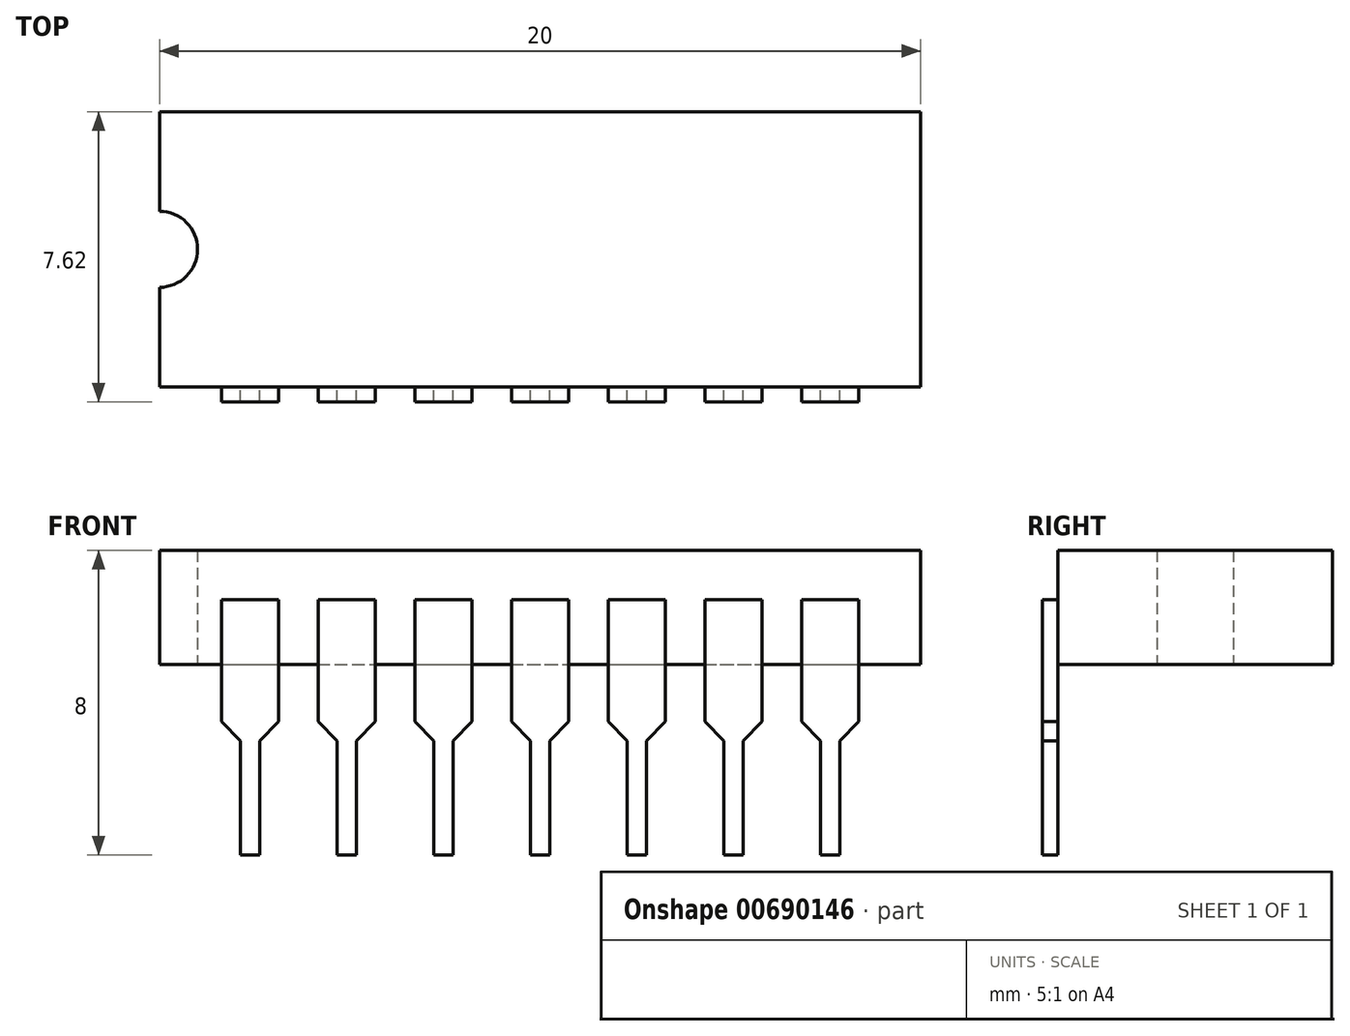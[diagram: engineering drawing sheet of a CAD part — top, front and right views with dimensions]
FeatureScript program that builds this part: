
annotation { "Feature Type Name" : "Feature", "Feature Type Description" : "" }
export const myFeature = defineFeature(function(context is Context, id is Id, definition is map)
    precondition{}
    {
        {
            var Q0;
            Q0=qCreatedBy(makeId("Top.planeOp"),FACE);
            var sketch = newSketch(context, id + "F0", { "sketchPlane" : qUnion([Q0])});
            skLineSegment(sketch, "E0.bottom", {"start": v(-10, 3.6) * mm, "end": v(10, 3.6) * mm});
            skLineSegment(sketch, "E0.top", {"start": v(-10, -3.6) * mm, "end": v(10, -3.6) * mm});
            skLineSegment(sketch, "E0.left", {"start": v(-10, 3.6) * mm, "end": v(-10, 1) * mm});
            skLineSegment(sketch, "E0.right", {"start": v(10, 3.6) * mm, "end": v(10, -3.6) * mm});
            skPoint(sketch, "E0.middle", {"position": v(0, 0) * mm});
            skArc(sketch, "E1", {"start": v(-10, 1) * mm, "mid": v(-9, 0) * mm, "end": v(-10, -1) * mm});
            skLineSegment(sketch, "E2.trimOffspring", {"start": v(-10, -1) * mm, "end": v(-10, -3.6) * mm});
            skSolve(sketch);
        }
        {
            var Q0;
            Q0 = qSketchRegion(id + "F0", true);
            extrude(context, id + "F1", {"entities" : qUnion([Q0]), "depth" : 5 * mm, "offsetDistance" : 25 * mm, "hasSecondDirection" : true, "secondDirectionOppositeDirection" : false, "secondDirectionDepth" : 2 * mm});
        }
        {
            var Q0;
            Q0=makeQuery(id+"F1.opExtrude","SWEPT_FACE",FACE,{"disambiguationData":[OSD([sQuery(id+"F0.wireOp",EDGE,"E0.top")])]});
            var sketch = newSketch(context, id + "F2", { "sketchPlane" : qUnion([Q0])});
            skLineSegment(sketch, "E3", {"start": v(-8.37, 3.7) * mm, "end": v(-8.37, 0.5) * mm});
            skLineSegment(sketch, "E4", {"start": v(-8.37, 0.5) * mm, "end": v(-7.87, 0) * mm});
            skLineSegment(sketch, "E5", {"start": v(-7.87, 0) * mm, "end": v(-7.87, -3) * mm});
            skLineSegment(sketch, "E6", {"start": v(-7.87, -3) * mm, "end": v(-7.37, -3) * mm});
            skLineSegment(sketch, "E7", {"start": v(-8.37, 3.7) * mm, "end": v(-6.87, 3.7) * mm});
            skLineSegment(sketch, "E8", {"start": v(-7.62, 3.7) * mm, "end": v(-7.62, -3) * mm, "construction": true});
            skLineSegment(sketch, "E9.MirrorCS", {"start": v(-7.37, 0) * mm, "end": v(-7.37, -3) * mm});
            skLineSegment(sketch, "E10.MirrorCS", {"start": v(-6.87, 3.7) * mm, "end": v(-6.87, 0.5) * mm});
            skLineSegment(sketch, "E11.MirrorCS", {"start": v(-6.87, 0.5) * mm, "end": v(-7.37, 0) * mm});
            skLineSegment(sketch, "E12.1.0.0", {"start": v(-5.33, 0) * mm, "end": v(-5.33, -3) * mm});
            skLineSegment(sketch, "E12.1.0.1", {"start": v(-5.08, 3.7) * mm, "end": v(-5.08, -3) * mm, "construction": true});
            skLineSegment(sketch, "E12.1.0.2", {"start": v(-4.33, 0.5) * mm, "end": v(-4.83, 0) * mm});
            skLineSegment(sketch, "E12.1.0.3", {"start": v(-4.33, 3.7) * mm, "end": v(-4.33, 0.5) * mm});
            skLineSegment(sketch, "E12.1.0.4", {"start": v(-5.83, 3.7) * mm, "end": v(-4.33, 3.7) * mm});
            skLineSegment(sketch, "E12.1.0.5", {"start": v(-5.83, 0.5) * mm, "end": v(-5.33, 0) * mm});
            skLineSegment(sketch, "E12.1.0.6", {"start": v(-4.83, 0) * mm, "end": v(-4.83, -3) * mm});
            skLineSegment(sketch, "E12.1.0.7", {"start": v(-5.83, 3.7) * mm, "end": v(-5.83, 0.5) * mm});
            skLineSegment(sketch, "E12.1.0.8", {"start": v(-5.33, -3) * mm, "end": v(-4.83, -3) * mm});
            skLineSegment(sketch, "E12.2.0.0", {"start": v(-2.79, 0) * mm, "end": v(-2.79, -3) * mm});
            skLineSegment(sketch, "E12.2.0.1", {"start": v(-2.54, 3.7) * mm, "end": v(-2.54, -3) * mm, "construction": true});
            skLineSegment(sketch, "E12.2.0.2", {"start": v(-1.79, 0.5) * mm, "end": v(-2.29, 0) * mm});
            skLineSegment(sketch, "E12.2.0.3", {"start": v(-1.79, 3.7) * mm, "end": v(-1.79, 0.5) * mm});
            skLineSegment(sketch, "E12.2.0.4", {"start": v(-3.29, 3.7) * mm, "end": v(-1.8, 3.7) * mm});
            skLineSegment(sketch, "E12.2.0.5", {"start": v(-3.29, 0.5) * mm, "end": v(-2.8, 0) * mm});
            skLineSegment(sketch, "E12.2.0.6", {"start": v(-2.29, 0) * mm, "end": v(-2.29, -3) * mm});
            skLineSegment(sketch, "E12.2.0.7", {"start": v(-3.29, 3.7) * mm, "end": v(-3.29, 0.5) * mm});
            skLineSegment(sketch, "E12.2.0.8", {"start": v(-2.79, -3) * mm, "end": v(-2.29, -3) * mm});
            skLineSegment(sketch, "E12.3.0.0", {"start": v(-0.25, 0) * mm, "end": v(-0.25, -3) * mm});
            skLineSegment(sketch, "E12.3.0.1", {"start": v(0, 3.7) * mm, "end": v(0, -3) * mm, "construction": true});
            skLineSegment(sketch, "E12.3.0.2", {"start": v(0.75, 0.5) * mm, "end": v(0.25, 0) * mm});
            skLineSegment(sketch, "E12.3.0.3", {"start": v(0.75, 3.7) * mm, "end": v(0.75, 0.5) * mm});
            skLineSegment(sketch, "E12.3.0.4", {"start": v(-0.75, 3.7) * mm, "end": v(0.75, 3.7) * mm});
            skLineSegment(sketch, "E12.3.0.5", {"start": v(-0.75, 0.5) * mm, "end": v(-0.25, 0) * mm});
            skLineSegment(sketch, "E12.3.0.6", {"start": v(0.25, 0) * mm, "end": v(0.25, -3) * mm});
            skLineSegment(sketch, "E12.3.0.7", {"start": v(-0.75, 3.7) * mm, "end": v(-0.75, 0.5) * mm});
            skLineSegment(sketch, "E12.3.0.8", {"start": v(-0.25, -3) * mm, "end": v(0.25, -3) * mm});
            skLineSegment(sketch, "E12.4.0.0", {"start": v(2.3, 0) * mm, "end": v(2.3, -3) * mm});
            skLineSegment(sketch, "E12.4.0.1", {"start": v(2.54, 3.7) * mm, "end": v(2.54, -3) * mm, "construction": true});
            skLineSegment(sketch, "E12.4.0.2", {"start": v(3.3, 0.5) * mm, "end": v(2.8, 0) * mm});
            skLineSegment(sketch, "E12.4.0.3", {"start": v(3.3, 3.7) * mm, "end": v(3.3, 0.5) * mm});
            skLineSegment(sketch, "E12.4.0.4", {"start": v(1.79, 3.7) * mm, "end": v(3.29, 3.7) * mm});
            skLineSegment(sketch, "E12.4.0.5", {"start": v(1.79, 0.5) * mm, "end": v(2.29, 0) * mm});
            skLineSegment(sketch, "E12.4.0.6", {"start": v(2.8, 0) * mm, "end": v(2.8, -3) * mm});
            skLineSegment(sketch, "E12.4.0.7", {"start": v(1.79, 3.7) * mm, "end": v(1.79, 0.5) * mm});
            skLineSegment(sketch, "E12.4.0.8", {"start": v(2.3, -3) * mm, "end": v(2.8, -3) * mm});
            skLineSegment(sketch, "E12.5.0.0", {"start": v(4.83, 0) * mm, "end": v(4.83, -3) * mm});
            skLineSegment(sketch, "E12.5.0.1", {"start": v(5.08, 3.7) * mm, "end": v(5.08, -3) * mm, "construction": true});
            skLineSegment(sketch, "E12.5.0.2", {"start": v(5.83, 0.5) * mm, "end": v(5.33, 0) * mm});
            skLineSegment(sketch, "E12.5.0.3", {"start": v(5.83, 3.7) * mm, "end": v(5.83, 0.5) * mm});
            skLineSegment(sketch, "E12.5.0.4", {"start": v(4.33, 3.7) * mm, "end": v(5.83, 3.7) * mm});
            skLineSegment(sketch, "E12.5.0.5", {"start": v(4.33, 0.5) * mm, "end": v(4.83, 0) * mm});
            skLineSegment(sketch, "E12.5.0.6", {"start": v(5.33, 0) * mm, "end": v(5.33, -3) * mm});
            skLineSegment(sketch, "E12.5.0.7", {"start": v(4.33, 3.7) * mm, "end": v(4.33, 0.5) * mm});
            skLineSegment(sketch, "E12.5.0.8", {"start": v(4.83, -3) * mm, "end": v(5.33, -3) * mm});
            skLineSegment(sketch, "E12.6.0.0", {"start": v(7.37, 0) * mm, "end": v(7.37, -3) * mm});
            skLineSegment(sketch, "E12.6.0.1", {"start": v(7.62, 3.7) * mm, "end": v(7.62, -3) * mm, "construction": true});
            skLineSegment(sketch, "E12.6.0.2", {"start": v(8.37, 0.5) * mm, "end": v(7.87, 0) * mm});
            skLineSegment(sketch, "E12.6.0.3", {"start": v(8.37, 3.7) * mm, "end": v(8.37, 0.5) * mm});
            skLineSegment(sketch, "E12.6.0.4", {"start": v(6.87, 3.7) * mm, "end": v(8.37, 3.7) * mm});
            skLineSegment(sketch, "E12.6.0.5", {"start": v(6.87, 0.5) * mm, "end": v(7.37, 0) * mm});
            skLineSegment(sketch, "E12.6.0.6", {"start": v(7.87, 0) * mm, "end": v(7.87, -3) * mm});
            skLineSegment(sketch, "E12.6.0.7", {"start": v(6.87, 3.7) * mm, "end": v(6.87, 0.5) * mm});
            skLineSegment(sketch, "E12.6.0.8", {"start": v(7.37, -3) * mm, "end": v(7.87, -3) * mm});
            skLineSegment(sketch, "E12.direction1", {"start": v(-7.87, -3) * mm, "end": v(-5.33, -3) * mm, "construction": true});
            skSolve(sketch);
        }
        {
            var Q0;
            Q0 = qSketchRegion(id + "F2", true);
            extrude(context, id + "F3", {"entities" : qUnion([Q0]), "operationType" : NewBodyOperationType.ADD, "depth" : 0.4 * mm, "offsetDistance" : 25 * mm});
        }
    });
